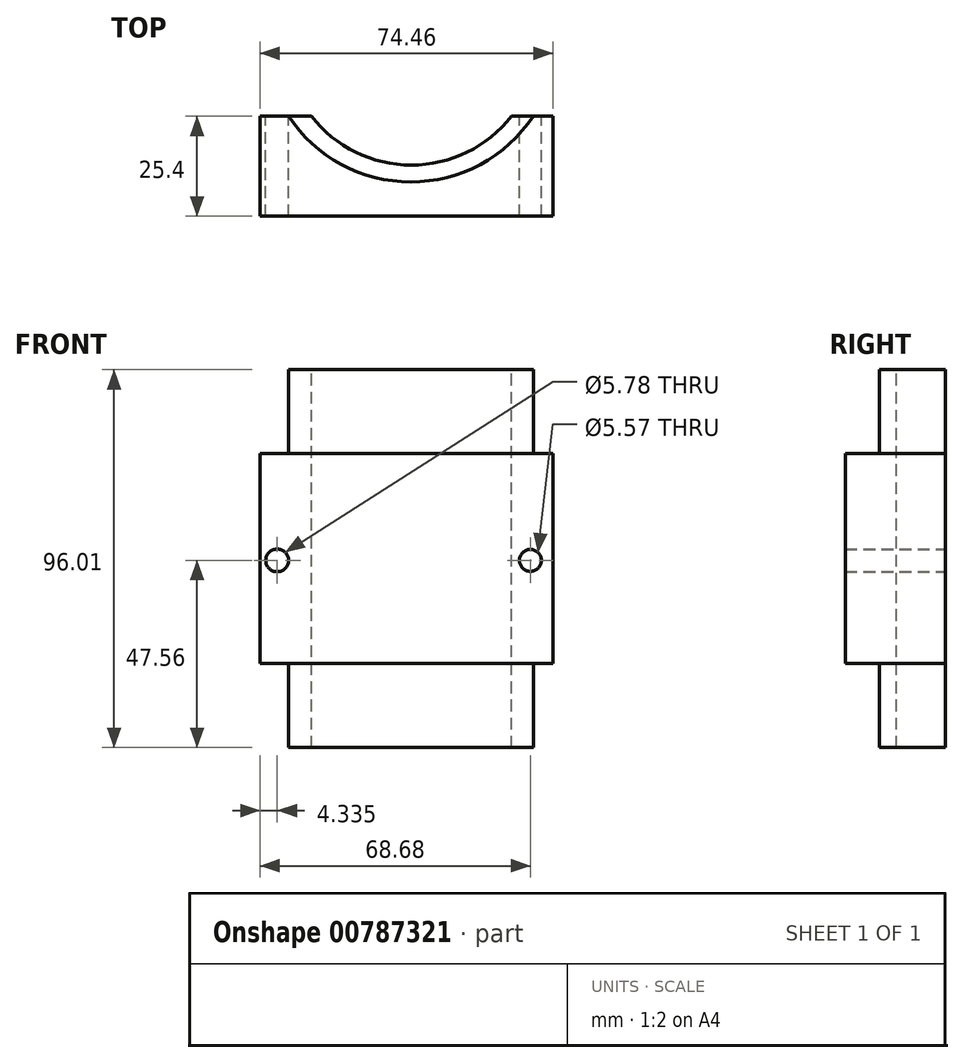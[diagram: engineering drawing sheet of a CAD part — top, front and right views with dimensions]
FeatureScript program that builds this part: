
annotation { "Feature Type Name" : "Feature", "Feature Type Description" : "" }
export const myFeature = defineFeature(function(context is Context, id is Id, definition is map)
    precondition{}
    {
        {
            var Q0;
            Q0=qCreatedBy(makeId("Front.planeOp"),FACE);
            var sketch = newSketch(context, id + "F0", { "sketchPlane" : qUnion([Q0])});
            skLineSegment(sketch, "E0.bottom", {"start": v(-27.35, 27.11) * mm, "end": v(47.11, 27.11) * mm});
            skLineSegment(sketch, "E0.top", {"start": v(-27.35, -26.15) * mm, "end": v(47.11, -26.15) * mm});
            skLineSegment(sketch, "E0.left", {"start": v(-27.35, 27.11) * mm, "end": v(-27.35, -26.15) * mm});
            skLineSegment(sketch, "E0.right", {"start": v(47.11, 27.11) * mm, "end": v(47.11, -26.15) * mm});
            skSolve(sketch);
        }
        {
            var Q0;
            Q0=makeQuery(id+"F0.imprint","IMPRINT",FACE,{"disambiguationData":[TD([[makeQuery(id+"F0.imprint","IMPRINT",EDGE,{"derivedFrom":sQuery(id+"F0.wireOp",EDGE,"E0.bottom")}),-1.0]])]});
            extrude(context, id + "F1", {"entities" : qUnion([Q0]), "depth" : 25.4 * mm, "offsetDistance" : 25.4 * mm});
        }
        {
            var Q0;
            Q0=makeQuery(id+"F1.opExtrude","SWEPT_FACE",FACE,{"disambiguationData":[OSD([sQuery(id+"F0.wireOp",EDGE,"E0.bottom")])]});
            var sketch = newSketch(context, id + "F2", { "sketchPlane" : qUnion([Q0])});
            skArc(sketch, "E1", {"start": v(-14.34, 0) * mm, "mid": v(11.09, -12.4) * mm, "end": v(36.51, 0) * mm});
            skLineSegment(sketch, "E2", {"start": v(-14.34, 0) * mm, "end": v(-20.12, 0) * mm});
            skLineSegment(sketch, "E3", {"start": v(36.51, 0) * mm, "end": v(42.05, 0) * mm});
            skArc(sketch, "E4", {"start": v(-20.12, 0) * mm, "mid": v(10.97, -16.7) * mm, "end": v(42.05, 0) * mm});
            skSolve(sketch);
        }
        {
            var Q0;
            Q0=makeQuery(id+"F2.imprint","IMPRINT",FACE,{"disambiguationData":[TD([[makeQuery(id+"F2.imprint","IMPRINT",EDGE,{"derivedFrom":sQuery(id+"F2.wireOp",EDGE,"E1")}),-1.0]])]});
            extrude(context, id + "F3", {"entities" : qUnion([Q0]), "operationType" : NewBodyOperationType.ADD, "oppositeDirection" : true, "depth" : 74.68 * mm, "offsetDistance" : 25.4 * mm});
        }
        {
            var Q0;
            Q0=makeQuery(id+"F3.opExtrude","CAP_FACE",FACE,{"disambiguationData":[OSD([sQuery(id+"F2.wireOp",EDGE,"E1"),sQuery(id+"F2.wireOp",EDGE,"E2"),sQuery(id+"F2.wireOp",EDGE,"E3"),sQuery(id+"F2.wireOp",EDGE,"E4")])],"isStart":false});
            extrude(context, id + "F4", {"entities" : qUnion([Q0]), "operationType" : NewBodyOperationType.ADD, "oppositeDirection" : true, "depth" : 96.01 * mm, "offsetDistance" : 25.4 * mm});
        }
        {
            var Q0;
            {var subQ2=sQuery(id+"F0.wireOp",EDGE,"E0.bottom");Q0=makeQuery(id+"F4.boolean.opBoolean","SPLIT",FACE,{"disambiguationData":[TD([makeQuery(id+"F4.opExtrude","SWEPT_FACE",FACE,{"disambiguationData":[OSD([sQuery(id+"F2.wireOp",EDGE,"E1")])]})])],"derivedFrom":makeQuery(id+"F1.opExtrude","SWEPT_FACE",FACE,{"disambiguationData":[OSD([subQ2])]})});}
            extrude(context, id + "F5", {"entities" : qUnion([Q0]), "operationType" : NewBodyOperationType.REMOVE, "oppositeDirection" : true, "depth" : 126.24 * mm, "offsetDistance" : 25.4 * mm});
        }
        {
            var Q0;
            {var subQ0=sQuery(id+"F0.wireOp",EDGE,"E0.left");var subQ3=sQuery(id+"F0.wireOp",EDGE,"E0.top");var subQ4=sQuery(id+"F2.wireOp",EDGE,"E3");var subQ5=sQuery(id+"F2.wireOp",EDGE,"E2");var subQ6=sQuery(id+"F0.wireOp",EDGE,"E0.bottom");Q0=makeQuery(id+"F5.boolean.opBoolean","SPLIT",FACE,{"disambiguationData":[TD([makeQuery(id+"F1.opExtrude","SWEPT_FACE",FACE,{"disambiguationData":[OSD([subQ0])]})])],"derivedFrom":makeQuery(id+"F4.boolean.opBoolean","MERGE",FACE,{"derivedFrom":[makeQuery(id+"F3.boolean.opBoolean","MERGE",FACE,{"derivedFrom":[makeQuery(id+"F1.opExtrude","CAP_FACE",FACE,{"disambiguationData":[OSD([subQ6,subQ3,subQ0,sQuery(id+"F0.wireOp",EDGE,"E0.right")])],"isStart":true}),makeQuery(id+"F3.opExtrude","SWEPT_FACE",FACE,{"disambiguationData":[OSD([subQ5])]}),makeQuery(id+"F3.opExtrude","SWEPT_FACE",FACE,{"disambiguationData":[OSD([subQ4])]})]}),makeQuery(id+"F4.opExtrude","SWEPT_FACE",FACE,{"disambiguationData":[OSD([subQ5])]}),makeQuery(id+"F4.opExtrude","SWEPT_FACE",FACE,{"disambiguationData":[OSD([subQ4])]})]})});}
            var sketch = newSketch(context, id + "F6", { "sketchPlane" : qUnion([Q0])});
            skCircle(sketch, "E5", {"center": v(23.01, 0) * mm, "radius": 2.9 * mm});
            skSolve(sketch);
        }
        {
            var Q0;
            Q0 = qSketchRegion(id + "F6", true);
            extrude(context, id + "F7", {"entities" : qUnion([Q0]), "operationType" : NewBodyOperationType.REMOVE, "oppositeDirection" : true, "depth" : 69.6 * mm, "offsetDistance" : 25.4 * mm});
        }
        {
            var Q0;
            {var subQ2=sQuery(id+"F0.wireOp",EDGE,"E0.top");var subQ3=sQuery(id+"F2.wireOp",EDGE,"E3");var subQ4=sQuery(id+"F2.wireOp",EDGE,"E2");var subQ5=sQuery(id+"F0.wireOp",EDGE,"E0.right");var subQ6=sQuery(id+"F0.wireOp",EDGE,"E0.bottom");Q0=makeQuery(id+"F5.boolean.opBoolean","SPLIT",FACE,{"disambiguationData":[TD([makeQuery(id+"F1.opExtrude","SWEPT_FACE",FACE,{"disambiguationData":[OSD([subQ5])]})])],"derivedFrom":makeQuery(id+"F4.boolean.opBoolean","MERGE",FACE,{"derivedFrom":[makeQuery(id+"F3.boolean.opBoolean","MERGE",FACE,{"derivedFrom":[makeQuery(id+"F1.opExtrude","CAP_FACE",FACE,{"disambiguationData":[OSD([subQ6,subQ2,sQuery(id+"F0.wireOp",EDGE,"E0.left"),subQ5])],"isStart":true}),makeQuery(id+"F3.opExtrude","SWEPT_FACE",FACE,{"disambiguationData":[OSD([subQ4])]}),makeQuery(id+"F3.opExtrude","SWEPT_FACE",FACE,{"disambiguationData":[OSD([subQ3])]})]}),makeQuery(id+"F4.opExtrude","SWEPT_FACE",FACE,{"disambiguationData":[OSD([subQ4])]}),makeQuery(id+"F4.opExtrude","SWEPT_FACE",FACE,{"disambiguationData":[OSD([subQ3])]})]})});}
            var sketch = newSketch(context, id + "F8", { "sketchPlane" : qUnion([Q0])});
            skCircle(sketch, "E6", {"center": v(-41.33, 0) * mm, "radius": 2.78 * mm});
            skSolve(sketch);
        }
        {
            var Q0;
            Q0=makeQuery(id+"F8.imprint","IMPRINT",FACE,{"disambiguationData":[TD([[makeQuery(id+"F8.imprint","IMPRINT",EDGE,{"derivedFrom":sQuery(id+"F8.wireOp",EDGE,"E6")}),1.0]])]});
            extrude(context, id + "F9", {"entities" : qUnion([Q0]), "operationType" : NewBodyOperationType.REMOVE, "oppositeDirection" : true, "depth" : 71.37 * mm, "offsetDistance" : 25.4 * mm});
        }
    });
